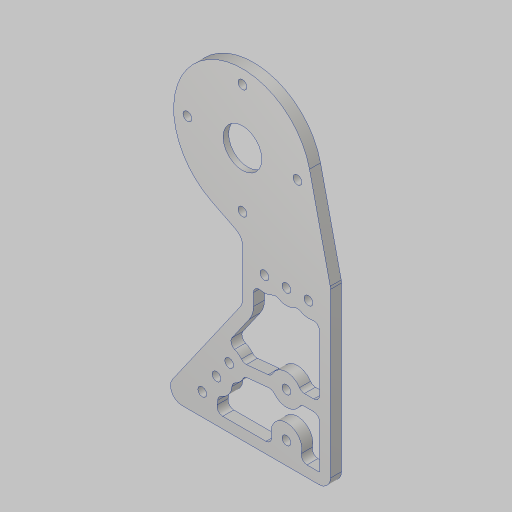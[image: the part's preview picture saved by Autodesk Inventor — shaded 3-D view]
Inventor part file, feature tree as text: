
AUTODESK INVENTOR PART (.ipt)
format: ipt  version: 2023.5 (Build 275446000, 446)  size: 310,784 bytes
history: native  units: in
note: dims shown in document units (in); Inventor stores cm internally (conversion verified against a paired STEP export)
features: sketch x5, extrude x3, hole x3, fillet x2, projected_geometry x2
ambient origin geometry x8: Origin, YZ Plane, XZ Plane, XY Plane, X Axis, Y Axis, Z Axis, Center Point
bodies: Solid1 (feature_tree)
feature tree (15):
  sketch  "Sketch1"  dims[d0=2.0in d1=15.25in]
  sketch  "Sketch2"  dims[d2=1.0in d3=17.0in d5=0.3779in]
  extrude  "Extrusion1"  Depth=15.25in
  hole  "Hole1"  [1 undecoded]
  fillet  "Fillet1"  Radius=0.3779in
  sketch  "Sketch3"  dims[d6=0.88in d7=1.875in]
  extrude  "Extrusion2"  Depth=1.875in
  hole  "Hole2"  [1 undecoded]
  hole  "Hole3"  [1 undecoded]
  extrude  "Extrusion3"  Depth=0.13in
  fillet  "Fillet2"  Radius=0.5in
  projected_geometry  "Projected Loop1"
  sketch  "Sketch4"  dims[d8=0.625in d11=17.0in]
  sketch  "Sketch5"  dims[d12=4.0in d13=1.0in d14=0.5in d15=0.5in d16=0.5655in d17=0.5in d18=0.25in d19=0.0in d20=0.201in d21=0.75in d22=0.385in d23=0.25in d24=0.5635in d25=1.0in d26=0.8108in d27=0.26in d28=1.875in d29=2.5in d30=1.5748in d32=360.0deg d34=0.125in d35=0.0in d36=0.201in d37=0.38in d38=0.385in d39=0.25in d40=0.5635in d41=1.0in d42=0.8108in d43=1.0in d44=0.5in d45=0.201in d46=0.38in d47=0.385in d48=0.25in d49=0.5635in d50=1.0in d51=0.8108in d52=2.0in d53=0.25in d54=0.25in d55=0.125in d56=0.0in d57=0.0in d60=0.125in d61=0.125in d62=0.13in]
  projected_geometry  "Projected Loop2"
note: 3 required parameter values undecoded (feature->parameter linkage not recoverable at this tier; creation-order binding heuristic only, values carry confidence <= 0.55)
